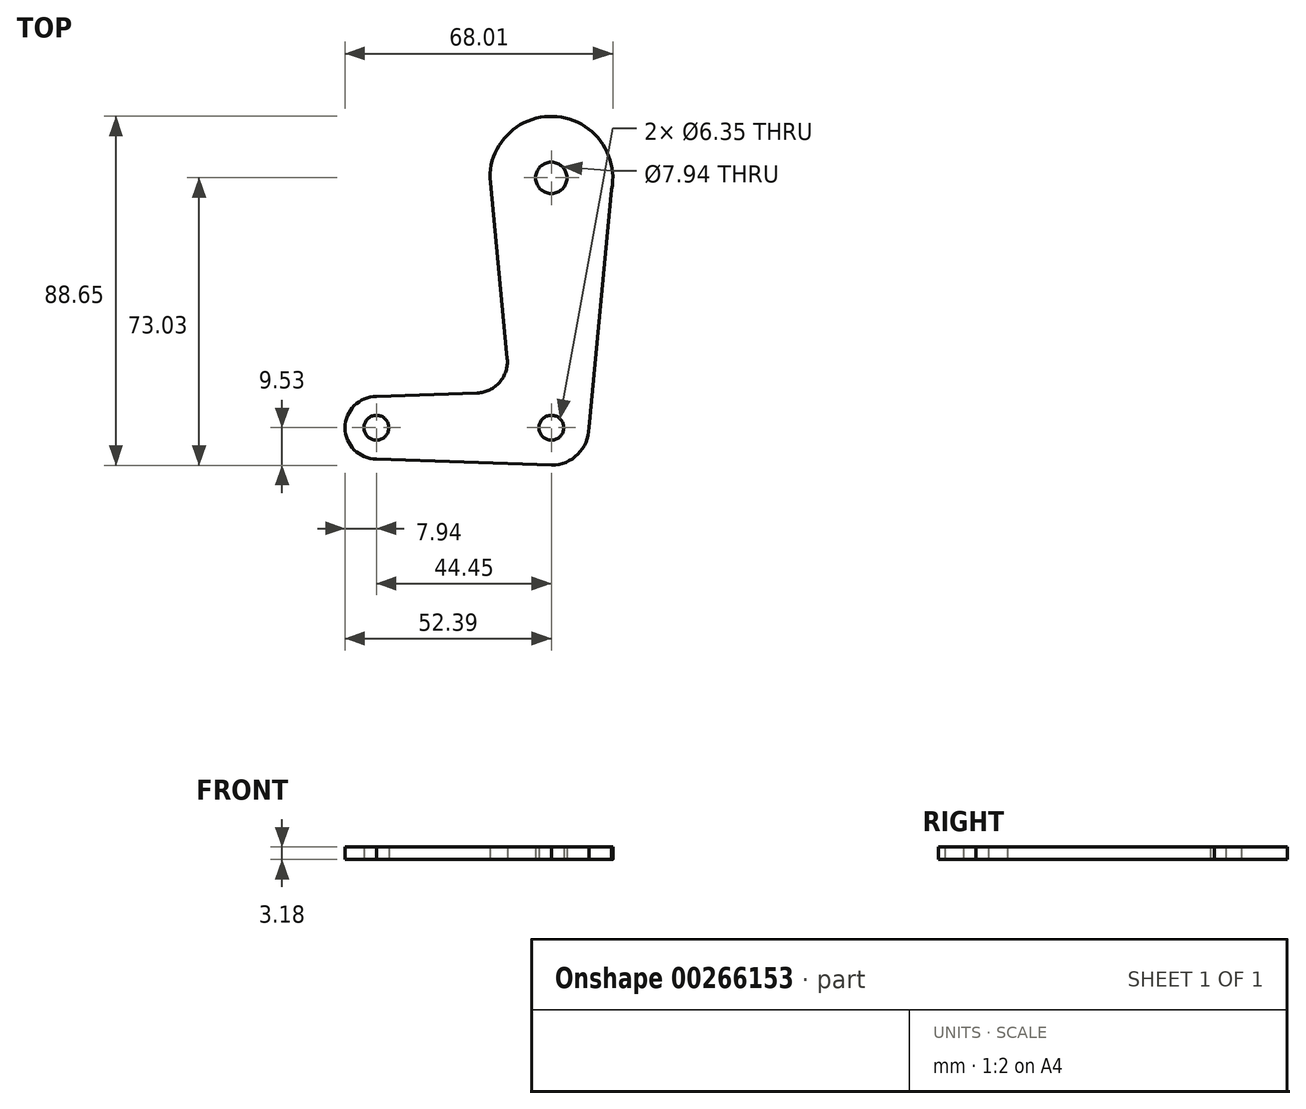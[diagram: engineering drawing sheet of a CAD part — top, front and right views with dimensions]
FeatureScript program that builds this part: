
annotation { "Feature Type Name" : "Feature", "Feature Type Description" : "" }
export const myFeature = defineFeature(function(context is Context, id is Id, definition is map)
    precondition{}
    {
        {
            var Q0;
            Q0=qCreatedBy(makeId("Top.planeOp"),FACE);
            var sketch = newSketch(context, id + "F0", { "sketchPlane" : qUnion([Q0])});
            skCircle(sketch, "E0", {"center": v(0, 0) * mm, "radius": 3.18 * mm});
            skCircle(sketch, "E1", {"center": v(44.45, 0) * mm, "radius": 3.18 * mm});
            skCircle(sketch, "E2", {"center": v(44.45, 63.5) * mm, "radius": 3.97 * mm});
            skArc(sketch, "E3", {"start": v(0, 7.94) * mm, "mid": v(-7.94, 0) * mm, "end": v(0, -7.94) * mm});
            skArc(sketch, "E4", {"start": v(43.77, -9.5) * mm, "mid": v(50.94, -6.97) * mm, "end": v(53.98, 0) * mm});
            skArc(sketch, "E5", {"start": v(59.79, 60.55) * mm, "mid": v(44.44, 79.12) * mm, "end": v(29.11, 60.53) * mm});
            skLineSegment(sketch, "E6", {"start": v(0, -7.94) * mm, "end": v(44.45, -9.53) * mm});
            skLineSegment(sketch, "E7", {"start": v(0, 7.94) * mm, "end": v(25.62, 8.85) * mm});
            skLineSegment(sketch, "E8", {"start": v(28.83, 63.5) * mm, "end": v(33.24, 17.54) * mm});
            skPoint(sketch, "E9.newPointA", {"position": v(44.45, 9.52) * mm});
            skPoint(sketch, "E9.newPointB", {"position": v(34.93, 0) * mm});
            skArc(sketch, "E9.filletArc", {"start": v(25.62, 8.85) * mm, "mid": v(31.3, 11.55) * mm, "end": v(33.24, 17.54) * mm});
            skLineSegment(sketch, "E10", {"start": v(53.97, 0) * mm, "end": v(59.79, 60.55) * mm});
            skSolve(sketch);
        }
        {
            var Q0;
            Q0=makeQuery(id+"F0.imprint","IMPRINT",FACE,{"disambiguationData":[TD([[makeQuery(id+"F0.imprint","IMPRINT",EDGE,{"derivedFrom":sQuery(id+"F0.wireOp",EDGE,"E0")}),-1.0]])]});
            extrude(context, id + "F1", {"entities" : qUnion([Q0]), "depth" : 3.17 * mm});
        }
    });
